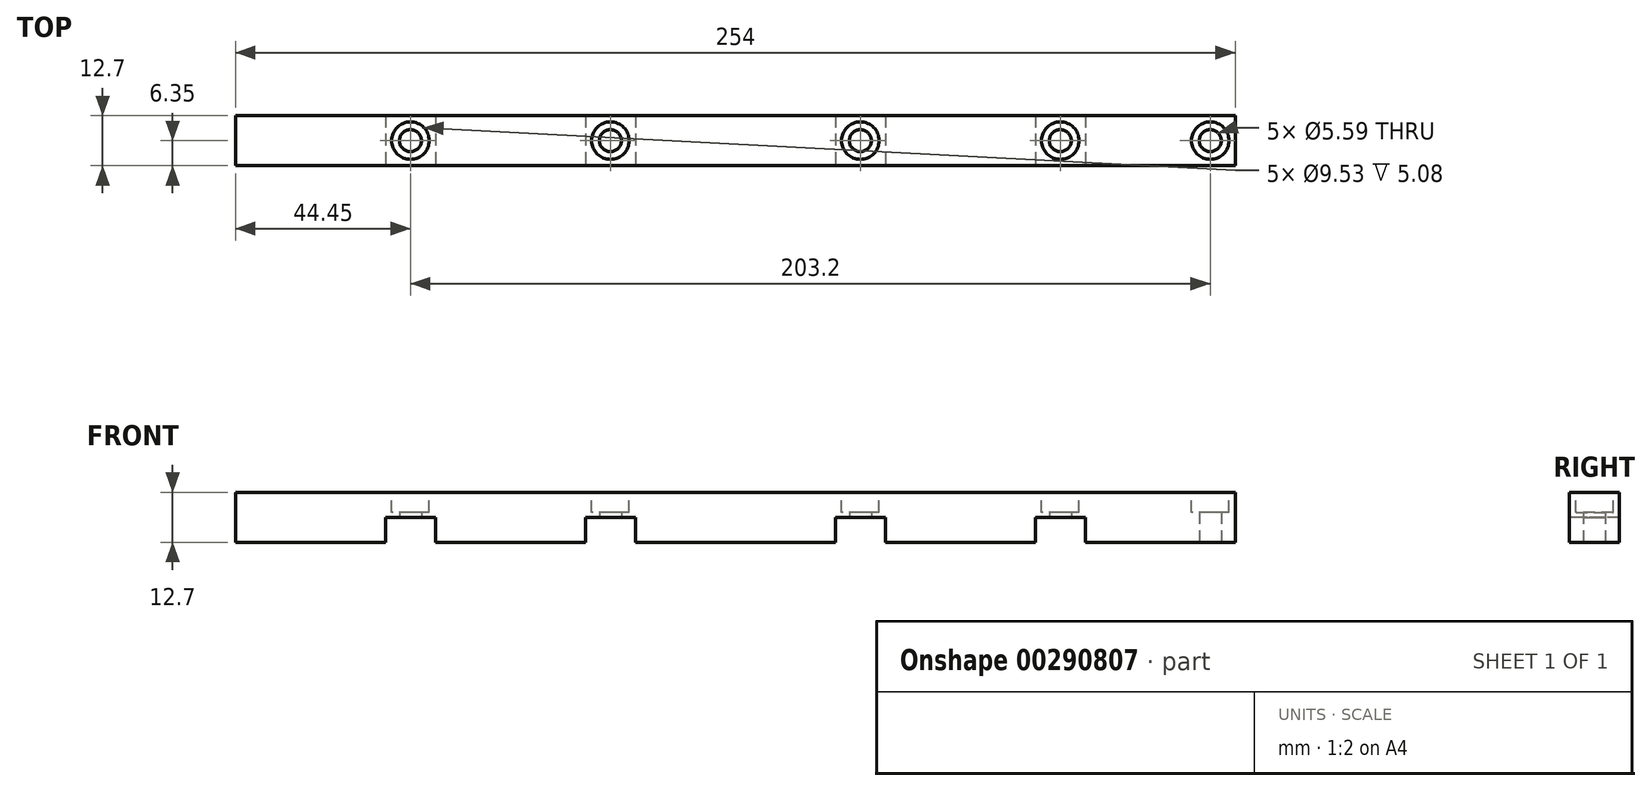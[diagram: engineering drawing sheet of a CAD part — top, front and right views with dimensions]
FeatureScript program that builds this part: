
annotation { "Feature Type Name" : "Feature", "Feature Type Description" : "" }
export const myFeature = defineFeature(function(context is Context, id is Id, definition is map)
    precondition{}
    {
        {
            var Q0;
            Q0=qCreatedBy(makeId("Top.planeOp"),FACE);
            var sketch = newSketch(context, id + "F0", { "sketchPlane" : qUnion([Q0])});
            skLineSegment(sketch, "E0.bottom", {"start": v(-127, 0) * mm, "end": v(127, 0) * mm});
            skLineSegment(sketch, "E0.top", {"start": v(-127, -12.7) * mm, "end": v(127, -12.7) * mm});
            skLineSegment(sketch, "E0.left", {"start": v(-127, 0) * mm, "end": v(-127, -12.7) * mm});
            skLineSegment(sketch, "E0.right", {"start": v(127, 0) * mm, "end": v(127, -12.7) * mm});
            skSolve(sketch);
        }
        {
            var Q0;
            Q0 = qSketchRegion(id + "F0", true);
            extrude(context, id + "F1", {"entities" : qUnion([Q0]), "depth" : 12.7 * mm});
        }
        {
            var Q0;
            Q0=makeQuery(id+"F1.opExtrude","SWEPT_FACE",FACE,{"disambiguationData":[OSD([sQuery(id+"F0.wireOp",EDGE,"E0.top")])]});
            var sketch = newSketch(context, id + "F2", { "sketchPlane" : qUnion([Q0])});
            skLineSegment(sketch, "E1.bottom", {"start": v(76.2, 6.35) * mm, "end": v(88.9, 6.35) * mm});
            skLineSegment(sketch, "E1.top", {"start": v(76.2, 0) * mm, "end": v(88.9, 0) * mm});
            skLineSegment(sketch, "E1.left", {"start": v(76.2, 6.35) * mm, "end": v(76.2, 0) * mm});
            skLineSegment(sketch, "E1.right", {"start": v(88.9, 6.35) * mm, "end": v(88.9, 0) * mm});
            skLineSegment(sketch, "E2.1.0.0", {"start": v(38.1, 6.35) * mm, "end": v(38.1, 0) * mm});
            skLineSegment(sketch, "E2.1.0.1", {"start": v(25.4, 0) * mm, "end": v(38.1, 0) * mm});
            skLineSegment(sketch, "E2.1.0.2", {"start": v(25.4, 6.35) * mm, "end": v(38.1, 6.35) * mm});
            skLineSegment(sketch, "E2.1.0.3", {"start": v(25.4, 6.35) * mm, "end": v(25.4, 0) * mm});
            skLineSegment(sketch, "E2.direction1", {"start": v(76.2, 0) * mm, "end": v(25.4, 0) * mm, "construction": true});
            skLineSegment(sketch, "E3.1.0.0", {"start": v(-38.1, 6.35) * mm, "end": v(-25.4, 6.35) * mm});
            skLineSegment(sketch, "E3.1.0.1", {"start": v(-76.2, 6.35) * mm, "end": v(-76.2, 0) * mm});
            skLineSegment(sketch, "E3.1.0.2", {"start": v(-88.9, 6.35) * mm, "end": v(-88.9, 0) * mm});
            skLineSegment(sketch, "E3.1.0.3", {"start": v(-25.4, 6.35) * mm, "end": v(-25.4, 0) * mm});
            skLineSegment(sketch, "E3.1.0.4", {"start": v(-38.1, 0) * mm, "end": v(-25.4, 0) * mm});
            skLineSegment(sketch, "E3.1.0.5", {"start": v(-88.9, 6.35) * mm, "end": v(-76.2, 6.35) * mm});
            skLineSegment(sketch, "E3.1.0.6", {"start": v(-88.9, 0) * mm, "end": v(-76.2, 0) * mm});
            skLineSegment(sketch, "E3.1.0.7", {"start": v(-38.1, 6.35) * mm, "end": v(-38.1, 0) * mm});
            skLineSegment(sketch, "E3.direction1", {"start": v(25.4, 0) * mm, "end": v(-88.9, 0) * mm, "construction": true});
            skSolve(sketch);
        }
        {
            var Q0;
            Q0 = qSketchRegion(id + "F2", true);
            extrude(context, id + "F3", {"entities" : qUnion([Q0]), "operationType" : NewBodyOperationType.REMOVE, "endBound" : BoundingType.THROUGH_ALL, "oppositeDirection" : true, "depth" : 25.4 * mm});
        }
        {
            var Q0;
            Q0=makeQuery(id+"F3.boolean.opBoolean","COPY",FACE,{"derivedFrom":makeQuery(id+"F3.opExtrude","SWEPT_FACE",FACE,{"disambiguationData":[OSD([sQuery(id+"F2.wireOp",EDGE,"E1.bottom")])]})});
            var sketch = newSketch(context, id + "F4", { "sketchPlane" : qUnion([Q0])});
            skCircle(sketch, "E4", {"center": v(82.55, 6.35) * mm, "radius": 2.8 * mm});
            skCircle(sketch, "E5.1.0.0", {"center": v(31.75, 6.35) * mm, "radius": 2.8 * mm});
            skLineSegment(sketch, "E5.direction1", {"start": v(82.55, 6.35) * mm, "end": v(31.75, 6.35) * mm, "construction": true});
            skCircle(sketch, "E6.1.0.0", {"center": v(-82.55, 6.35) * mm, "radius": 2.8 * mm});
            skCircle(sketch, "E6.1.0.1", {"center": v(-31.75, 6.35) * mm, "radius": 2.8 * mm});
            skLineSegment(sketch, "E6.direction1", {"start": v(31.75, 6.35) * mm, "end": v(-82.55, 6.35) * mm, "construction": true});
            skSolve(sketch);
        }
        {
            var Q0;
            Q0 = qSketchRegion(id + "F4", true);
            extrude(context, id + "F5", {"entities" : qUnion([Q0]), "operationType" : NewBodyOperationType.REMOVE, "endBound" : BoundingType.THROUGH_ALL, "oppositeDirection" : true, "depth" : 25.4 * mm});
        }
        {
            var Q0;
            Q0=makeQuery(id+"F1.opExtrude","CAP_FACE",FACE,{"disambiguationData":[OSD([sQuery(id+"F0.wireOp",EDGE,"E0.bottom"),sQuery(id+"F0.wireOp",EDGE,"E0.top"),sQuery(id+"F0.wireOp",EDGE,"E0.left"),sQuery(id+"F0.wireOp",EDGE,"E0.right")])],"isStart":false});
            var sketch = newSketch(context, id + "F6", { "sketchPlane" : qUnion([Q0])});
            skCircle(sketch, "E7", {"center": v(82.55, -6.35) * mm, "radius": 4.76 * mm});
            skCircle(sketch, "E8.1.0.0", {"center": v(31.75, -6.35) * mm, "radius": 4.76 * mm});
            skLineSegment(sketch, "E8.direction1", {"start": v(82.55, -6.35) * mm, "end": v(31.75, -6.35) * mm, "construction": true});
            skCircle(sketch, "E9.1.0.0", {"center": v(-82.55, -6.35) * mm, "radius": 4.76 * mm});
            skCircle(sketch, "E9.1.0.1", {"center": v(-31.75, -6.35) * mm, "radius": 4.76 * mm});
            skLineSegment(sketch, "E9.direction1", {"start": v(31.75, -6.35) * mm, "end": v(-82.55, -6.35) * mm, "construction": true});
            skSolve(sketch);
        }
        {
            var Q0;
            Q0 = qSketchRegion(id + "F6", true);
            extrude(context, id + "F7", {"entities" : qUnion([Q0]), "operationType" : NewBodyOperationType.REMOVE, "oppositeDirection" : true, "depth" : 5.08 * mm});
        }
        {
            var Q0;
            {var subQ0=sQuery(id+"F0.wireOp",EDGE,"E0.bottom");var subQ1=sQuery(id+"F0.wireOp",EDGE,"E0.right");var subQ2=sQuery(id+"F0.wireOp",EDGE,"E0.top");Q0=makeQuery(id+"F3.boolean.opBoolean","SPLIT",FACE,{"disambiguationData":[TD([makeQuery(id+"F1.opExtrude","SWEPT_FACE",FACE,{"disambiguationData":[OSD([subQ1])]})])],"derivedFrom":makeQuery(id+"F1.opExtrude","CAP_FACE",FACE,{"disambiguationData":[OSD([subQ0,subQ2,sQuery(id+"F0.wireOp",EDGE,"E0.left"),subQ1])],"isStart":true})});}
            var sketch = newSketch(context, id + "F8", { "sketchPlane" : qUnion([Q0])});
            skCircle(sketch, "E10", {"center": v(120.65, 6.35) * mm, "radius": 2.8 * mm});
            skSolve(sketch);
        }
        {
            var Q0;
            Q0 = qSketchRegion(id + "F8", true);
            extrude(context, id + "F9", {"entities" : qUnion([Q0]), "operationType" : NewBodyOperationType.REMOVE, "endBound" : BoundingType.THROUGH_ALL, "oppositeDirection" : true, "depth" : 25.4 * mm});
        }
        {
            var Q0;
            Q0=makeQuery(id+"F1.opExtrude","CAP_FACE",FACE,{"disambiguationData":[OSD([sQuery(id+"F0.wireOp",EDGE,"E0.bottom"),sQuery(id+"F0.wireOp",EDGE,"E0.top"),sQuery(id+"F0.wireOp",EDGE,"E0.left"),sQuery(id+"F0.wireOp",EDGE,"E0.right")])],"isStart":false});
            var sketch = newSketch(context, id + "F10", { "sketchPlane" : qUnion([Q0])});
            skCircle(sketch, "E11", {"center": v(120.65, -6.35) * mm, "radius": 4.76 * mm});
            skSolve(sketch);
        }
        {
            var Q0;
            Q0=makeQuery(id+"F10.imprint","IMPRINT",FACE,{"disambiguationData":[TD([[makeQuery(id+"F10.imprint","IMPRINT",EDGE,{"derivedFrom":sQuery(id+"F10.wireOp",EDGE,"E11")}),1.0]])]});
            extrude(context, id + "F11", {"entities" : qUnion([Q0]), "operationType" : NewBodyOperationType.REMOVE, "oppositeDirection" : true, "depth" : 5.08 * mm});
        }
    });
